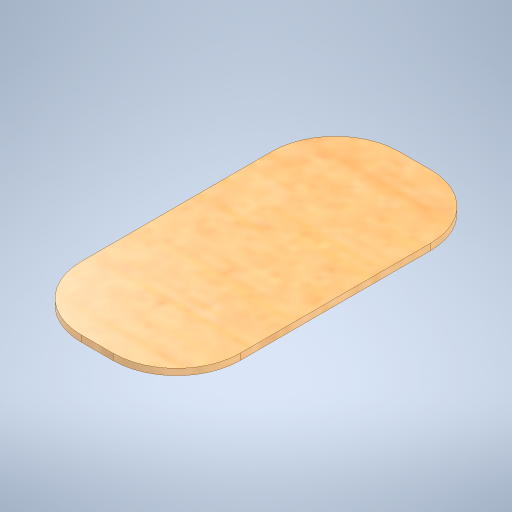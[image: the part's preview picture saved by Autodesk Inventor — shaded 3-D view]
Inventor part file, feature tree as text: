
AUTODESK INVENTOR PART (.ipt)
format: ipt  version: 2023 (Build 270158000, 158)  size: 284,672 bytes
history: native  units: in
note: dims shown in document units (in); Inventor stores cm internally (conversion verified against a paired STEP export)
features: extrude x1, sketch x1
ambient origin geometry x8: Origin, YZ Plane, XZ Plane, XY Plane, X Axis, Y Axis, Z Axis, Center Point
bodies: Solid1 (feature_tree)
feature tree (2):
  extrude  "Extrusion1"  Depth=1.9685in
  sketch  "Sketch1"  dims[d0=0.9843in d1=1.9685in d2=0.0787in d3=0.3937in d4=0.0394in d5=0.0in]
